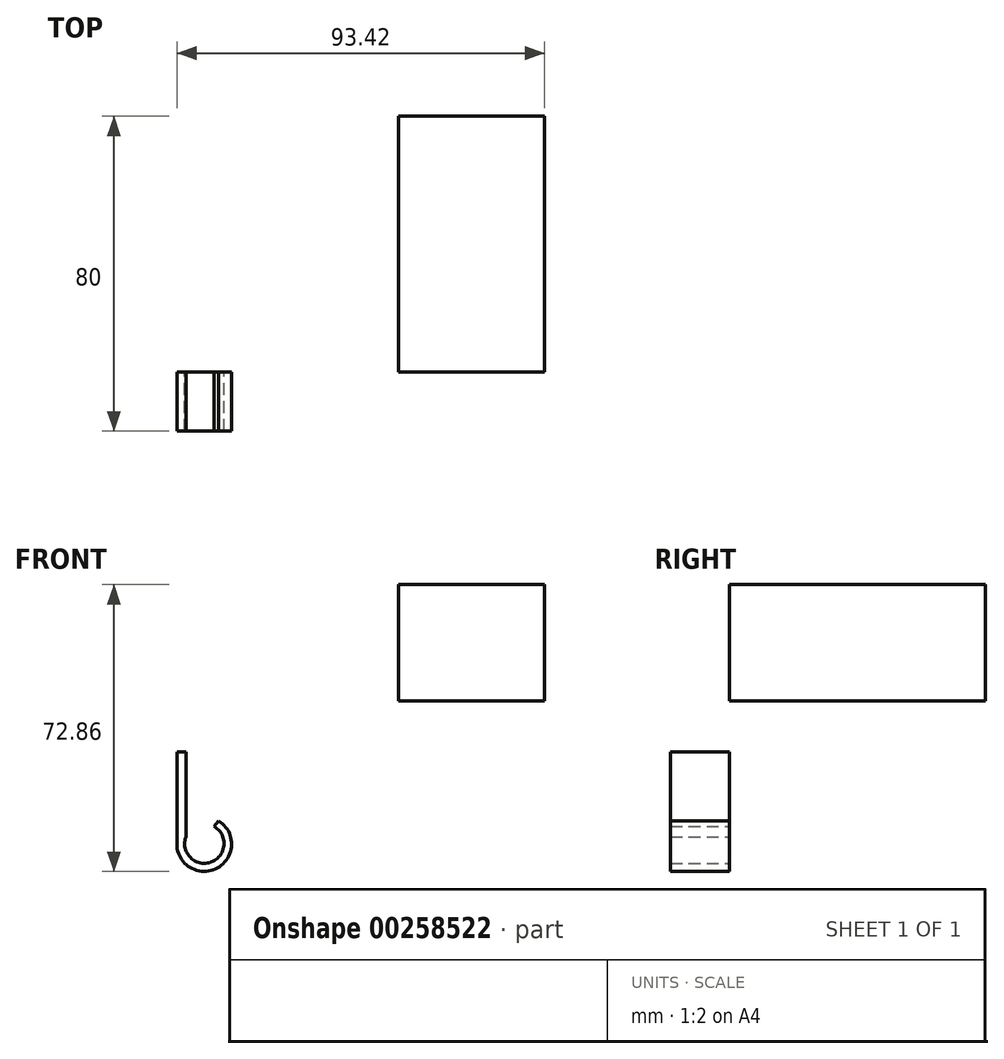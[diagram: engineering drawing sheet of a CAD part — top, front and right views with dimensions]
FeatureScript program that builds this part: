
annotation { "Feature Type Name" : "Feature", "Feature Type Description" : "" }
export const myFeature = defineFeature(function(context is Context, id is Id, definition is map)
    precondition{}
    {
        {
            var Q0;
            Q0=qCreatedBy(makeId("Front.planeOp"),FACE);
            var sketch = newSketch(context, id + "F0", { "sketchPlane" : qUnion([Q0])});
            skLineSegment(sketch, "E0", {"start": v(-48.6, -12.9) * mm, "end": v(-48.6, -36.3) * mm});
            skArc(sketch, "E1", {"start": v(-48.6, -36.3) * mm, "mid": v(-38.28, -42.38) * mm, "end": v(-37.96, -30.41) * mm});
            skLineSegment(sketch, "E2", {"start": v(-48.6, -12.9) * mm, "end": v(-46.3, -12.9) * mm});
            skLineSegment(sketch, "E3", {"start": v(-46.3, -12.9) * mm, "end": v(-46.3, -34.5) * mm});
            skArc(sketch, "E4", {"start": v(-46.3, -34.5) * mm, "mid": v(-39.9, -40.91) * mm, "end": v(-39.1, -31.88) * mm});
            skLineSegment(sketch, "E5", {"start": v(-37.96, -30.41) * mm, "end": v(-39.1, -31.88) * mm});
            skSolve(sketch);
        }
        {
            var Q0;
            Q0=makeQuery(id+"F0.imprint","IMPRINT",FACE,{"disambiguationData":[TD([[makeQuery(id+"F0.imprint","IMPRINT",EDGE,{"derivedFrom":sQuery(id+"F0.wireOp",EDGE,"E0")}),1.0]])]});
            extrude(context, id + "F1", {"entities" : qUnion([Q0]), "depth" : 15 * mm});
        }
        {
            var Q0;
            Q0=qCreatedBy(makeId("Front.planeOp"),FACE);
            var sketch = newSketch(context, id + "F3", { "sketchPlane" : qUnion([Q0])});
            skLineSegment(sketch, "E6.bottom", {"start": v(44.82, 29.6) * mm, "end": v(7.79, 29.6) * mm});
            skLineSegment(sketch, "E6.top", {"start": v(44.82, 0) * mm, "end": v(7.79, 0) * mm});
            skLineSegment(sketch, "E6.left", {"start": v(44.82, 29.6) * mm, "end": v(44.82, 0) * mm});
            skLineSegment(sketch, "E6.right", {"start": v(7.79, 29.6) * mm, "end": v(7.79, 0) * mm});
            skSolve(sketch);
        }
        {
            var Q0;
            Q0=makeQuery(id+"F3.imprint","IMPRINT",FACE,{"disambiguationData":[TD([[makeQuery(id+"F3.imprint","IMPRINT",EDGE,{"derivedFrom":sQuery(id+"F3.wireOp",EDGE,"E6.bottom")}),1.0]])]});
            extrude(context, id + "F2", {"entities" : qUnion([Q0]), "oppositeDirection" : true, "depth" : 65 * mm});
        }
    });
